# Revit family: SDD75X93
name_source: partatom
category: Detail Items
revit_build: Autodesk Revit 2015 (Build: 20140606_1530(x64)
units: mm (PartAtom-declared; Revit-internal decimal feet)

## types (2) — shared parameters
Density = 0.03 kg
Description = Self-Drilling Dowel
EPD = https://www.strongtie.eu
ETA / DoP = https://www.strongtie.eu
Manufacturer = Simpson Strong-Tie
Model = SDD7.5X93
Model Disclaimer = Contact Simpson Strong-Tie Company  for more information
Model ID = 0265537266666926939334260751448800469312
Name = SDD7.5X93
ObjectType = SDD7.5X93
Product Material = ElectroGalvanised
Product Type = Self-Drilling Dowel
Reference = 78119
Technical datasheet = https://www.strongtie.eu
URL = www.strongtie.eu
UniClass Number = Pr_20_29_76_76
UniClass Title = Self-drilling screws

## per-type parameters (varying)
| type | _visiblefront | _visibletop |
| SST_SDD7.5X93_Top | No | Yes |
| SST_SDD7.5X93_Front | Yes | No |

## geometry (parser evidence)
native form markers: Blend x2, Sweep x1
no freeform markers — native parametric forms only
